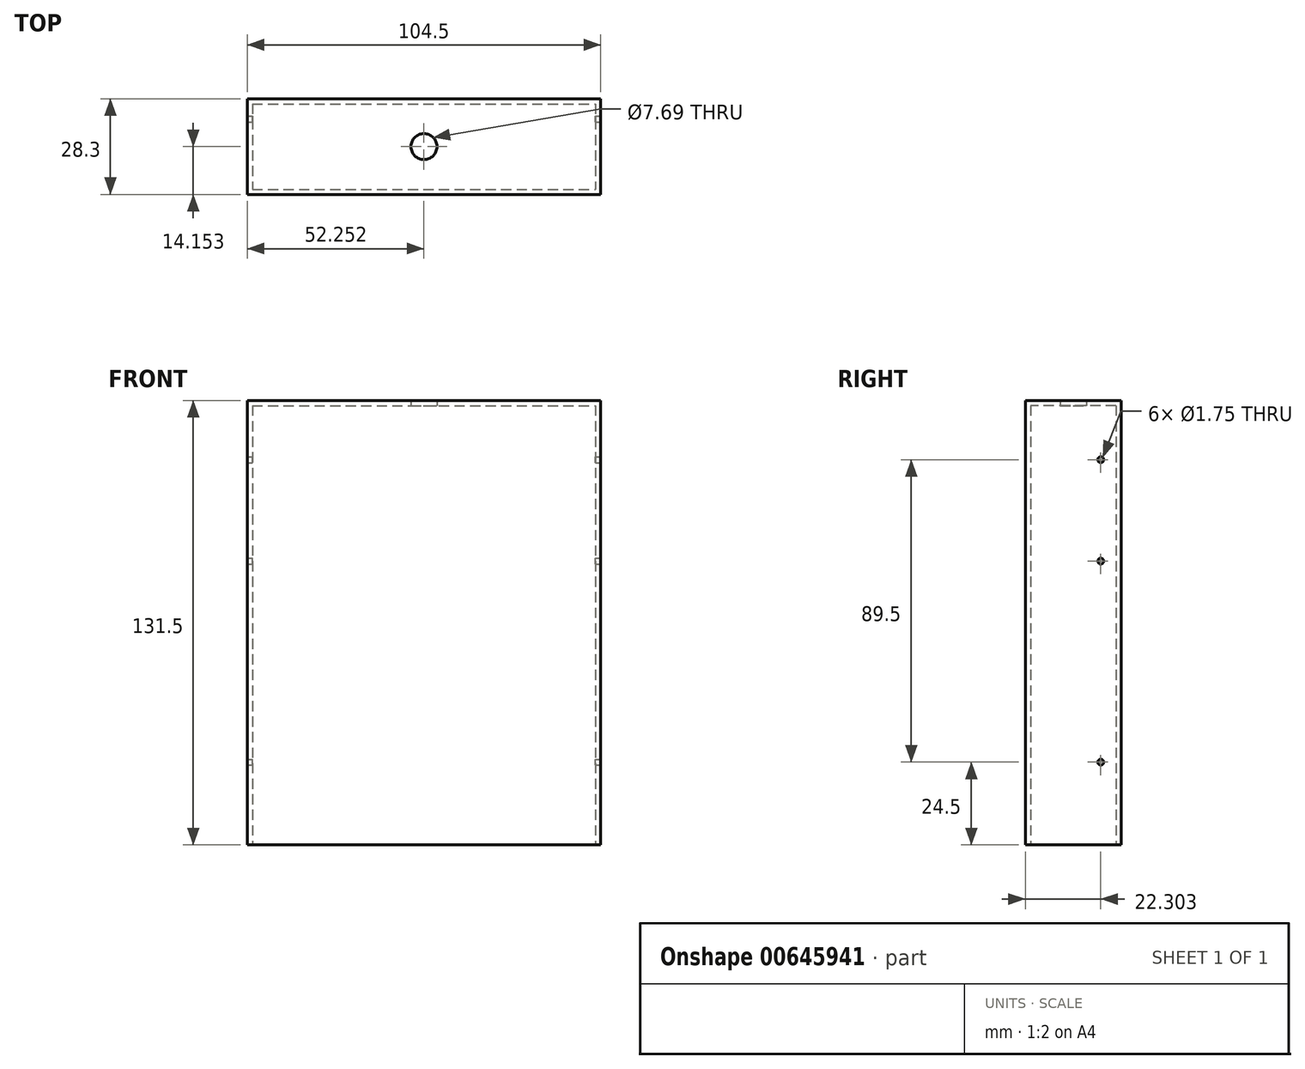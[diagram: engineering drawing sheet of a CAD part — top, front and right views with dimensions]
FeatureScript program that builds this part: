
annotation { "Feature Type Name" : "Feature", "Feature Type Description" : "" }
export const myFeature = defineFeature(function(context is Context, id is Id, definition is map)
    precondition{}
    {
        {
            var Q0;
            Q0=qCreatedBy(makeId("Top.planeOp"),FACE);
            var sketch = newSketch(context, id + "F0", { "sketchPlane" : qUnion([Q0])});
            skLineSegment(sketch, "E0.bottom", {"start": v(-53.58, 10.08) * mm, "end": v(47.92, 10.08) * mm});
            skLineSegment(sketch, "E0.top", {"start": v(-53.58, -15.22) * mm, "end": v(47.92, -15.22) * mm});
            skLineSegment(sketch, "E0.left", {"start": v(-53.58, 10.08) * mm, "end": v(-53.58, -15.22) * mm});
            skLineSegment(sketch, "E0.right", {"start": v(47.92, 10.08) * mm, "end": v(47.92, -15.22) * mm});
            skLineSegment(sketch, "E1.0", {"start": v(-55.08, 11.58) * mm, "end": v(-55.08, -16.72) * mm});
            skLineSegment(sketch, "E1.1", {"start": v(-55.08, 11.58) * mm, "end": v(49.42, 11.58) * mm});
            skLineSegment(sketch, "E1.2", {"start": v(49.42, 11.58) * mm, "end": v(49.42, -16.72) * mm});
            skLineSegment(sketch, "E1.3", {"start": v(-55.08, -16.72) * mm, "end": v(49.42, -16.72) * mm});
            skSolve(sketch);
        }
        {
            var Q0;
            Q0=makeQuery(id+"F0.imprint","IMPRINT",FACE,{"disambiguationData":[TD([[makeQuery(id+"F0.imprint","IMPRINT",EDGE,{"derivedFrom":sQuery(id+"F0.wireOp",EDGE,"E0.bottom")}),1.0]])]});
            extrude(context, id + "F1", {"entities" : qUnion([Q0]), "depth" : 130 * mm, "offsetDistance" : 25 * mm});
        }
        {
            var Q0;
            Q0=makeQuery(id+"F1.opExtrude","SWEPT_FACE",FACE,{"disambiguationData":[OSD([sQuery(id+"F0.wireOp",EDGE,"E1.2")])]});
            var sketch = newSketch(context, id + "F2", { "sketchPlane" : qUnion([Q0])});
            skCircle(sketch, "E2", {"center": v(5.58, 24.5) * mm, "radius": 0.87 * mm});
            skLineSegment(sketch, "E3", {"start": v(5.58, 24.5) * mm, "end": v(5.58, 143.5) * mm, "construction": true});
            skCircle(sketch, "E4", {"center": v(5.58, 84) * mm, "radius": 0.87 * mm});
            skCircle(sketch, "E5", {"center": v(5.58, 114) * mm, "radius": 0.88 * mm});
            skSolve(sketch);
        }
        {
            var Q0;
            Q0=makeQuery(id+"F2.imprint","IMPRINT",FACE,{"disambiguationData":[TD([[makeQuery(id+"F2.imprint","IMPRINT",EDGE,{"derivedFrom":sQuery(id+"F2.wireOp",EDGE,"E5")}),1.0]])]});
            var Q1;
            Q1=makeQuery(id+"F2.imprint","IMPRINT",FACE,{"disambiguationData":[TD([[makeQuery(id+"F2.imprint","IMPRINT",EDGE,{"derivedFrom":sQuery(id+"F2.wireOp",EDGE,"E4")}),1.0]])]});
            var Q2;
            Q2=makeQuery(id+"F2.imprint","IMPRINT",FACE,{"disambiguationData":[TD([[makeQuery(id+"F2.imprint","IMPRINT",EDGE,{"derivedFrom":sQuery(id+"F2.wireOp",EDGE,"E2")}),1.0]])]});
            var Q3;
            Q3=sQuery(id+"F2.wireOp",EDGE,"E5");
            var Q4;
            Q4=sQuery(id+"F2.wireOp",EDGE,"E4");
            var Q5;
            Q5=sQuery(id+"F2.wireOp",EDGE,"E2");
            extrude(context, id + "F3", {"entities" : qUnion([Q0, Q1, Q2]), "operationType" : NewBodyOperationType.REMOVE, "surfaceEntities" : qUnion([Q3, Q4, Q5]), "oppositeDirection" : true, "depth" : 130 * mm, "offsetDistance" : 25 * mm});
        }
        {
            var Q0;
            Q0=makeQuery(id+"F1.opExtrude","CAP_FACE",FACE,{"disambiguationData":[OSD([sQuery(id+"F0.wireOp",EDGE,"E0.bottom"),sQuery(id+"F0.wireOp",EDGE,"E0.top"),sQuery(id+"F0.wireOp",EDGE,"E0.left"),sQuery(id+"F0.wireOp",EDGE,"E0.right"),sQuery(id+"F0.wireOp",EDGE,"E1.0"),sQuery(id+"F0.wireOp",EDGE,"E1.1"),sQuery(id+"F0.wireOp",EDGE,"E1.2"),sQuery(id+"F0.wireOp",EDGE,"E1.3")])],"isStart":false});
            var sketch = newSketch(context, id + "F4", { "sketchPlane" : qUnion([Q0])});
            skLineSegment(sketch, "E6.bottom", {"start": v(-55.08, 11.58) * mm, "end": v(49.42, 11.58) * mm});
            skLineSegment(sketch, "E6.top", {"start": v(-55.08, -16.72) * mm, "end": v(49.42, -16.72) * mm});
            skLineSegment(sketch, "E6.left", {"start": v(-55.08, 11.58) * mm, "end": v(-55.08, -16.72) * mm});
            skLineSegment(sketch, "E6.right", {"start": v(49.42, 11.58) * mm, "end": v(49.42, -16.72) * mm});
            skSolve(sketch);
        }
        {
            var Q0;
            Q0 = qSketchRegion(id + "F4", true);
            extrude(context, id + "F5", {"entities" : qUnion([Q0]), "operationType" : NewBodyOperationType.ADD, "depth" : 1.5 * mm, "offsetDistance" : 25 * mm});
        }
        {
            var Q0;
            Q0=makeQuery(id+"F5.opExtrude","CAP_FACE",FACE,{"disambiguationData":[OSD([sQuery(id+"F4.wireOp",EDGE,"E6.bottom"),sQuery(id+"F4.wireOp",EDGE,"E6.top"),sQuery(id+"F4.wireOp",EDGE,"E6.left"),sQuery(id+"F4.wireOp",EDGE,"E6.right")])],"isStart":true});
            var sketch = newSketch(context, id + "F6", { "sketchPlane" : qUnion([Q0])});
            skCircle(sketch, "E7", {"center": v(-2.83, 2.57) * mm, "radius": 3.85 * mm});
            skSolve(sketch);
        }
        {
            var Q0;
            Q0 = qSketchRegion(id + "F6", true);
            extrude(context, id + "F7", {"entities" : qUnion([Q0]), "operationType" : NewBodyOperationType.REMOVE, "oppositeDirection" : true, "depth" : 3 * mm, "offsetDistance" : 25 * mm});
        }
    });
